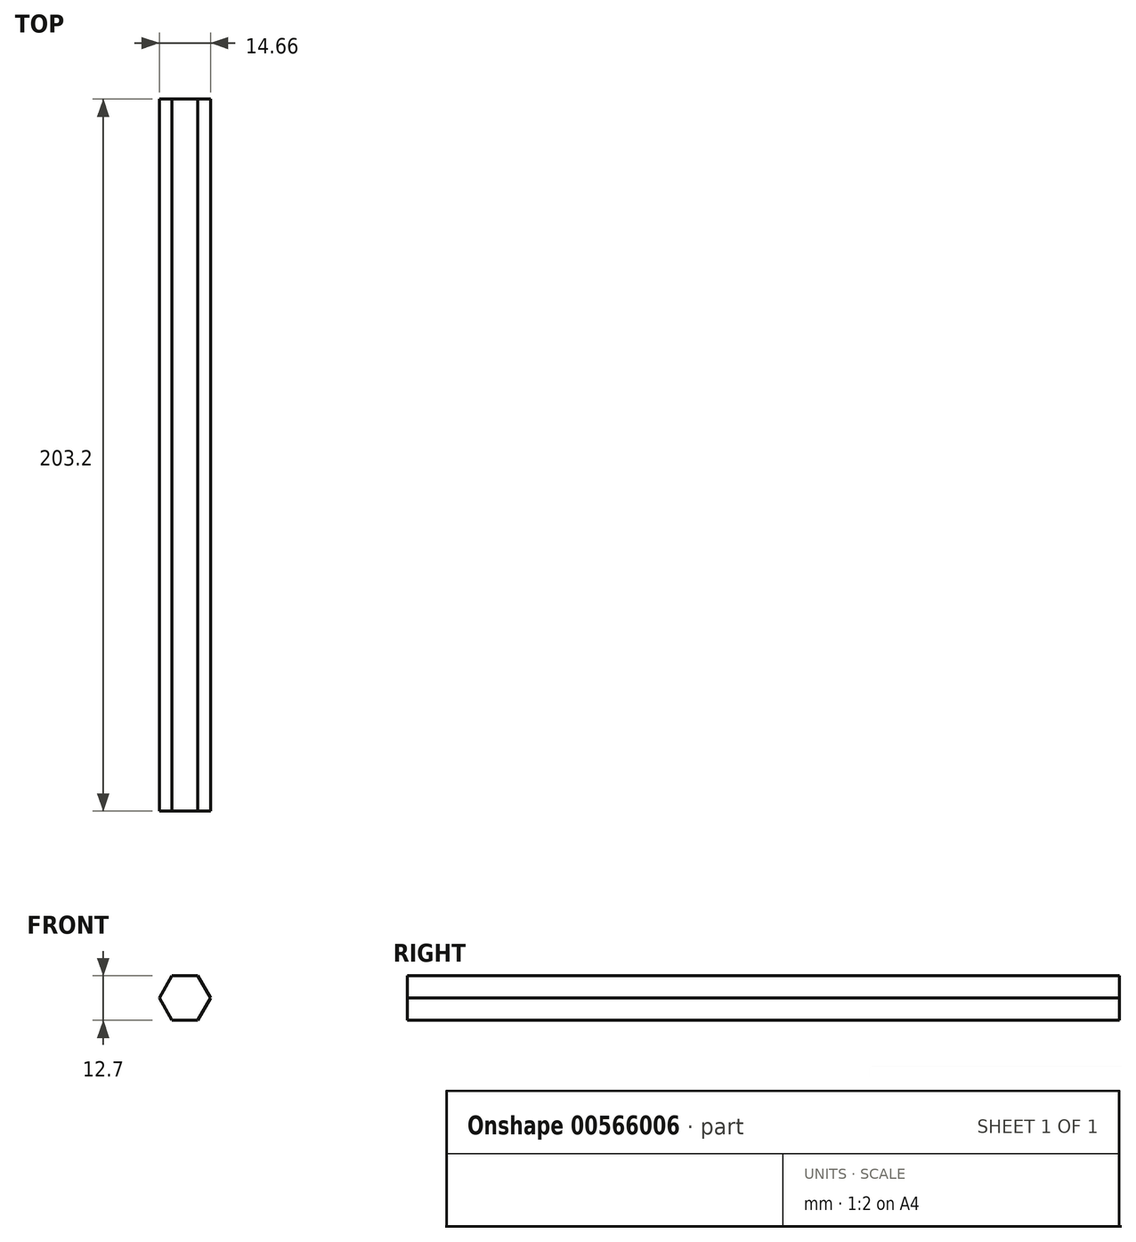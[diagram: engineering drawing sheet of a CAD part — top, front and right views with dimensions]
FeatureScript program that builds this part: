
annotation { "Feature Type Name" : "Feature", "Feature Type Description" : "" }
export const myFeature = defineFeature(function(context is Context, id is Id, definition is map)
    precondition{}
    {
        {
            var Q0;
            Q0=qCreatedBy(makeId("Front.planeOp"),FACE);
            var sketch = newSketch(context, id + "F0", { "sketchPlane" : qUnion([Q0])});
            skCircle(sketch, "E0.cCircle", {"center": v(0, 0) * mm, "radius": 6.35 * mm, "construction": true});
            skLineSegment(sketch, "E0.0", {"start": v(7.33, 0) * mm, "end": v(3.67, -6.35) * mm});
            skLineSegment(sketch, "E0.1", {"start": v(3.67, -6.35) * mm, "end": v(-3.67, -6.35) * mm});
            skLineSegment(sketch, "E0.2", {"start": v(-3.67, -6.35) * mm, "end": v(-7.33, 0) * mm});
            skLineSegment(sketch, "E0.3", {"start": v(-7.33, 0) * mm, "end": v(-3.67, 6.35) * mm});
            skLineSegment(sketch, "E0.4", {"start": v(-3.67, 6.35) * mm, "end": v(3.67, 6.35) * mm});
            skLineSegment(sketch, "E0.5", {"start": v(3.67, 6.35) * mm, "end": v(7.33, 0) * mm});
            skPoint(sketch, "E0.0.midPoint", {"position": v(5.5, -3.18) * mm});
            skSolve(sketch);
        }
        {
            var Q0;
            Q0=makeQuery(id+"F0.imprint","IMPRINT",FACE,{"disambiguationData":[TD([[makeQuery(id+"F0.imprint","IMPRINT",EDGE,{"derivedFrom":sQuery(id+"F0.wireOp",EDGE,"E0.0")}),-1.0]])]});
            extrude(context, id + "F1", {"entities" : qUnion([Q0]), "depth" : 203.2 * mm, "offsetDistance" : 25.4 * mm});
        }
    });
